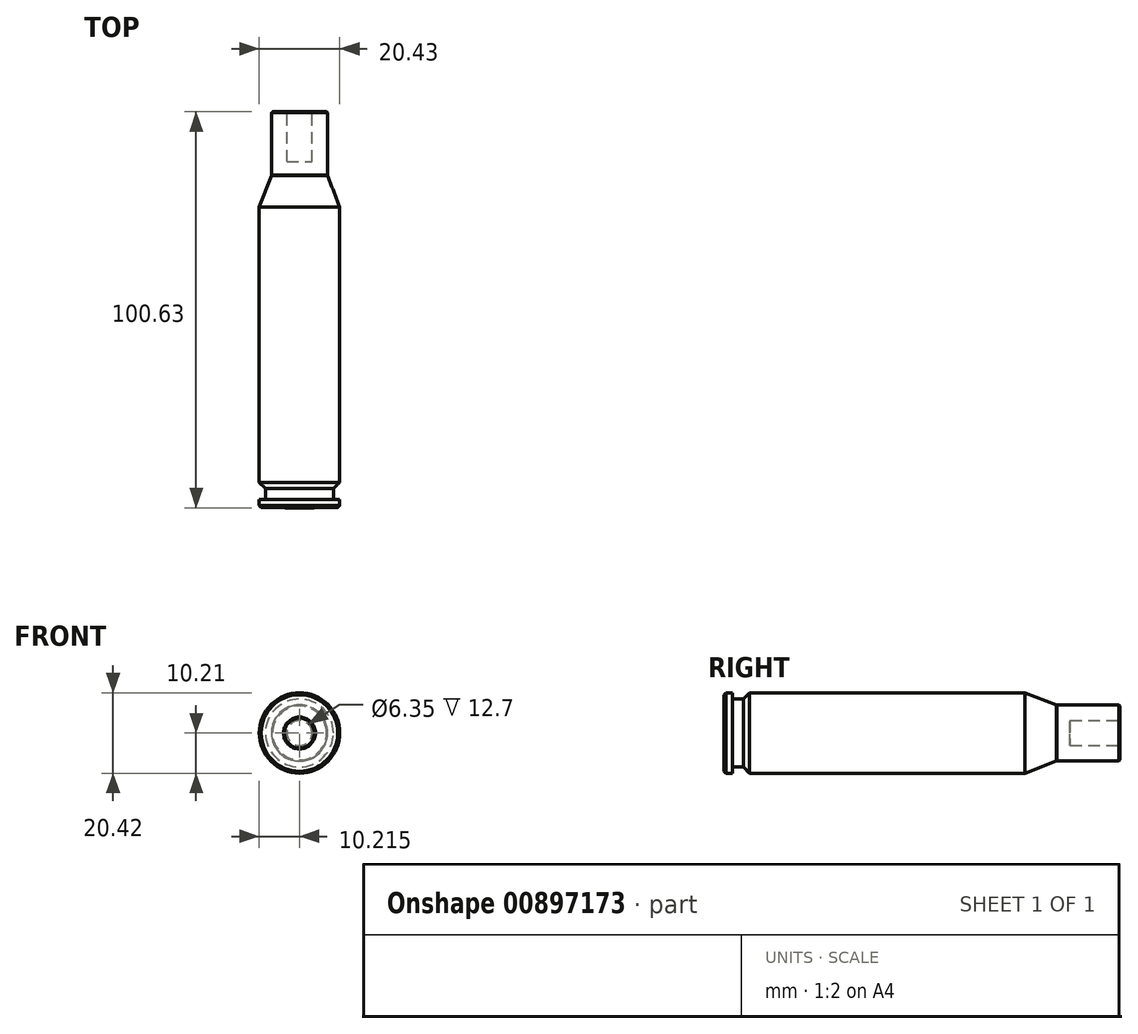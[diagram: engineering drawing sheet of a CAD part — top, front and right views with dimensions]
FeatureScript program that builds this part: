
annotation { "Feature Type Name" : "Feature", "Feature Type Description" : "" }
export const myFeature = defineFeature(function(context is Context, id is Id, definition is map)
    precondition{}
    {
        {
            var Q0;
            Q0=qCreatedBy(makeId("Top.planeOp"),FACE);
            var sketch = newSketch(context, id + "F0", { "sketchPlane" : qUnion([Q0])});
            skLineSegment(sketch, "E0", {"start": v(-15.33, -69.1) * mm, "end": v(-19.13, -69.1) * mm});
            skLineSegment(sketch, "E1", {"start": v(-19.13, -69.1) * mm, "end": v(-19.13, -74.49) * mm});
            skLineSegment(sketch, "E2", {"start": v(-15.33, -74.45) * mm, "end": v(-25.54, -74.45) * mm});
            skLineSegment(sketch, "E3", {"start": v(-25.54, -74.45) * mm, "end": v(-25.54, -72.34) * mm});
            skLineSegment(sketch, "E4", {"start": v(-25.54, -72.34) * mm, "end": v(-23.96, -72.34) * mm});
            skLineSegment(sketch, "E5", {"start": v(-23.96, -72.34) * mm, "end": v(-23.96, -69.58) * mm});
            skLineSegment(sketch, "E6", {"start": v(-23.96, -69.58) * mm, "end": v(-25.54, -68) * mm});
            skLineSegment(sketch, "E7", {"start": v(-25.54, -68) * mm, "end": v(-25.54, 1.9) * mm});
            skLineSegment(sketch, "E8", {"start": v(-22.44, 10.04) * mm, "end": v(-22.44, 26.14) * mm});
            skLineSegment(sketch, "E9", {"start": v(-25.54, -68) * mm, "end": v(-25.54, -70.26) * mm});
            skLineSegment(sketch, "E10", {"start": v(-25.54, 1.9) * mm, "end": v(-22.44, 10.04) * mm});
            skLineSegment(sketch, "E11", {"start": v(-22.44, 26.14) * mm, "end": v(-21.45, 26.14) * mm});
            skLineSegment(sketch, "E12", {"start": v(-15.36, 37.48) * mm, "end": v(-21.85, 37.48) * mm});
            skLineSegment(sketch, "E13", {"start": v(-21.85, 37.48) * mm, "end": v(-21.85, 26.82) * mm});
            skFitSpline(sketch, "E14", {"points": [v(-21.85, 26.82) * mm, v(-21.45, 26.14) * mm], "startDerivative": vector(0, -1.61) * mm, "endDerivative": vector(1.35, -2.86) * mm});
            skLineSegment(sketch, "E15", {"start": v(-18.44, 58.8) * mm, "end": v(-21.44, 44.27) * mm});
            skFitSpline(sketch, "E16", {"points": [v(-21.85, 37.48) * mm, v(-21.44, 44.27) * mm], "startDerivative": vector(-0.07, 5.87) * mm, "endDerivative": vector(1.37, 5.74) * mm});
            skLineSegment(sketch, "E17", {"start": v(-15.33, 62.7) * mm, "end": v(-15.33, 26.14) * mm});
            skLineSegment(sketch, "E18", {"start": v(-15.33, -74.45) * mm, "end": v(-15.33, 26.14) * mm});
            skLineSegment(sketch, "E19", {"start": v(-21.45, 26.14) * mm, "end": v(-15.33, 26.14) * mm});
            skFitSpline(sketch, "E20", {"points": [v(-18.44, 58.8) * mm, v(-15.33, 62.7) * mm], "startDerivative": vector(1.9, 4.77) * mm, "endDerivative": vector(3.4, 0.19) * mm});
            skSolve(sketch);
        }
        {
            var Q0;
            {var subQ0=sQuery(id+"F0.wireOp",EDGE,"E0");Q0=makeQuery(id+"F0.imprint","IMPRINT",FACE,{"disambiguationData":[TD([[makeQuery(id+"F0.imprint","IMPRINT",EDGE,{"derivedFrom":subQ0}),-1.0]])]});}
            var Q1;
            {var subQ1=sQuery(id+"F0.wireOp",EDGE,"E12");Q1=makeQuery(id+"F0.imprint","IMPRINT",FACE,{"disambiguationData":[TD([[makeQuery(id+"F0.imprint","IMPRINT",EDGE,{"derivedFrom":subQ1}),1.0]])]});}
            var Q2;
            {var subQ1=sQuery(id+"F0.wireOp",EDGE,"E12");Q2=makeQuery(id+"F0.imprint","IMPRINT",FACE,{"disambiguationData":[TD([[makeQuery(id+"F0.imprint","IMPRINT",EDGE,{"derivedFrom":subQ1}),-1.0]])]});}
            var Q3;
            Q3=sQuery(id+"F0.wireOp",EDGE,"E18");
            revolve(context, id + "F1", {"surfaceOperationType" : NewSurfaceOperationType.NEW, "entities" : qUnion([Q0, Q1, Q2]), "axis" : qUnion([Q3]), "revolveType" : RevolveType.FULL});
        }
        {
            var Q0;
            Q0=makeQuery(id+"F1.opRevolve","SWEPT_EDGE",EDGE,{"disambiguationData":[OSD([sQuery(id+"F0.wireOp",EDGE,"E1"),sQuery(id+"F0.wireOp",EDGE,"E2")])]});
            var Q1;
            Q1=makeQuery(id+"F1.opRevolve","SWEPT_EDGE",EDGE,{"disambiguationData":[OSD([sQuery(id+"F0.wireOp",EDGE,"E8"),sQuery(id+"F0.wireOp",EDGE,"88vX6Dcv-yaL2-YR9K-8U8G-9htzLIJxvQV1")])]});
            chamfer(context, id + "F2", {"entities" : qUnion([Q0, Q1]), "width" : 0.25 * mm, "tangentPropagation" : true});
        }
        {
            var Q0;
            Q0=makeQuery(id+"F1.opRevolve","SWEPT_FACE",FACE,{"disambiguationData":[OSD([sQuery(id+"F0.wireOp",EDGE,"E0")])]});
            extrude(context, id + "F3", {"entities" : qUnion([Q0]), "operationType" : NewBodyOperationType.ADD, "depth" : 5.38 * mm, "offsetDistance" : 25.4 * mm});
        }
        {
            var Q0;
            Q0=makeQuery(id+"F3.opExtrude","CAP_EDGE",EDGE,{"disambiguationData":[OSD([sQuery(id+"F0.wireOp",EDGE,"E0"),sQuery(id+"F0.wireOp",EDGE,"E1")])],"isStart":false});
            fillet(context, id + "F4", {"entities" : qUnion([Q0]), "radius" : 0.25 * mm, "tangentPropagation" : true, "allowEdgeOverflow" : false});
        }
        {
            var Q0;
            Q0=makeQuery(id+"F1.opRevolve","SWEPT_EDGE",EDGE,{"disambiguationData":[OSD([sQuery(id+"F0.wireOp",EDGE,"E2"),sQuery(id+"F0.wireOp",EDGE,"E3")])]});
            chamfer(context, id + "F5", {"entities" : qUnion([Q0]), "width" : 0.5 * mm, "tangentPropagation" : true});
        }
        {
            var Q0;
            Q0=makeQuery(id+"F1.opRevolve","SWEPT_FACE",FACE,{"disambiguationData":[OSD([sQuery(id+"F0.wireOp",EDGE,"E11"),sQuery(id+"F0.wireOp",EDGE,"E19")])]});
            var sketch = newSketch(context, id + "F6", { "sketchPlane" : qUnion([Q0])});
            skCircle(sketch, "E21", {"center": v(15.33, 0) * mm, "radius": 3.18 * mm});
            skSolve(sketch);
        }
        {
            var Q0;
            Q0=makeQuery(id+"F6.imprint","IMPRINT",FACE,{"disambiguationData":[TD([[makeQuery(id+"F6.imprint","IMPRINT",EDGE,{"derivedFrom":sQuery(id+"F6.wireOp",EDGE,"E21")}),1.0]])]});
            extrude(context, id + "F7", {"entities" : qUnion([Q0]), "operationType" : NewBodyOperationType.REMOVE, "oppositeDirection" : true, "depth" : 12.7 * mm, "offsetDistance" : 25.4 * mm});
        }
    });
